# Revit family: DA330, DA420
name_source: partatom
category: Mechanical Equipment
revit_build: Autodesk Revit 2017 (Build: 20181011_1645(x64)
units: mm (PartAtom-declared; Revit-internal decimal feet)

## family parameters
Always vertical = Yes
Cut with Voids When Loaded = No
OmniClass Number = 23.40.40.11.17
OmniClass Title = Refrigerated Cases
Part Type = Normal
Room Calculation Point = No
Round Connector Dimension = Use Radius
Shared = No
Work Plane-Based = Yes

## types (1)
- D330, D420
    10" Shelf = Yes
    16" Shelf = Yes
    24" Shelf = Yes
    AIR-SWEEP FAN AMPS = 0 A
    Actual Weight = 0
    BOTTOM ELECTRICAL = Yes
    BOTTOM REFRIGERATION PIPING = Yes
    COLD WATER FILTER REQUIRED = Yes
    COLD WATER MOUNTING HEIGHT = 0"
    COLD WATER PIPE SIZE = 0"
    COLD WATER PRESSURE = 0.00 psi
    COLD WATER REGULATOR REQUIRED = Yes
    DATE = 09/03/2017
    DESIGNERS NAME = SHIDDRAMESH
    DRAIN LINE CONNECTION = SANITARY LINE CONNECTION
    DRAIN PIPING = Yes
    DUCT 1 CFM = 0 CFM
    DUCT 1 OPENING SIZE = 0"
    Default Elevation = 48"
    Defrost Num Day = 0
    Defrost Termination = -
    Defrost Type = -
    Description = SoloChill Condensing Unit
    EQUIPMENT DESCRIPTION = SoloChill Condensing Unit
    EQUIPMENT MARK = D330, D420
    Evap Temp = 0
    FAN AMPS = 1 A
    GLASS = Glass
    HOT WATER MOUNTING HEIGHT = 0"
    HOT WATER PIPE SIZE = 0"
    HOT WATER PRESSURE = 0.00 psi
    HOT WATER REGULATOR REQUIRED = Yes
    HOT WATER TEMPERATURE = 0 °F
    Height = 12 3/16"
    Item Description = SoloChill Condensing Unit
    LF STD END = Yes
    LIGHT AMPS = 0 A
    LIQUID LINE CONNECTION = LIQUID LINE CONNECTION
    LIQUID LINE RADIUS = 0"
    LOAD 1 CLASSIFICATION = Lighting
    LOAD 1 DEDICATED CIRCUIT REQUIRED = Yes
    LOAD 1 DESCRIPTION = LIGHT CONNECTION
    LOAD 1 ENERGY SETBACK REQUIRED = Yes
    LOAD 1 GROUND FAULT PROTECTION REQUIRED = Yes
    LOAD 1 ISOLATED GROUND REQUIRED = Yes
    LOAD 1 MOUNTING HEIGHT ABOVE FLOOR = 0"
    LOAD 1 NEUTRAL REQUIRED = Yes
    LOAD 1 POLES = 1
    LOAD 1 VOLTAGE = 120 V
    LOAD 1 WATTAGE = 0 W
    LOAD 2 CLASSIFICATION = Motor
    LOAD 2 DEDICATED CIRCUIT REQUIRED = Yes
    LOAD 2 DESCRIPTION = FAN CONNECTION
    LOAD 2 ENERGY SETBACK REQUIRED = Yes
    LOAD 2 GROUND FAULT PROTECTION REQUIRED = Yes
    LOAD 2 ISOLATED GROUND REQUIRED = Yes
    LOAD 2 MOUNTING HEIGHT ABOVE FLOOR = 0"
    LOAD 2 NEUTRAL REQUIRED = Yes
    LOAD 2 PLUG TYPE = HARDWIRED
    LOAD 2 POLES = 1
    LOAD 2 VOLTAGE = 120 V
    LOAD 2 WATTAGE = 0 W
    LOAD 3 CLASSIFICATION = Power
    LOAD 3 DEDICATED CIRCUIT REQUIRED = Yes
    LOAD 3 DESCRIPTION = ANTI-SWEAT CONNECTION
    LOAD 3 ENERGY SETBACK REQUIRED = Yes
    LOAD 3 GROUND FAULT PROTECTION REQUIRED = Yes
    LOAD 3 ISOLATED GROUND REQUIRED = Yes
    LOAD 3 MOUNTING HEIGHT ABOVE FLOOR = 0"
    LOAD 3 NEUTRAL REQUIRED = Yes
    LOAD 3 PLUG TYPE = HARDWIRED
    LOAD 3 POLES = 1
    LOAD 3 VOLTAGE = 120 V
    LOAD 3 WATTAGE = 0 W
    LOAD 4 CLASSIFICATION = Power
    LOAD 4 DEDICATED CIRCUIT REQUIRED = Yes
    LOAD 4 DESCRIPTION = DEFROST CONNECTION
    LOAD 4 ENERGY SETBACK REQUIRED = Yes
    LOAD 4 GROUND FAULT PROTECTION REQUIRED = Yes
    LOAD 4 ISOLATED GROUND REQUIRED = Yes
    LOAD 4 MOUNTING HEIGHT ABOVE FLOOR = 0"
    LOAD 4 NEUTRAL REQUIRED = Yes
    LOAD 4 PLUG TYPE = HARDWIRED
    LOAD 4 POLES = 1
    LOAD 4 VOLTAGE = 208 V
    LOAD 4 WATTAGE = 0 W
    LOAD 5 CLASSIFICATION = Power
    LOAD 5 DEDICATED CIRCUIT REQUIRED = Yes
    LOAD 5 DESCRIPTION = DRAIN HEATER CONNECTION
    LOAD 5 ENERGY SETBACK REQUIRED = Yes
    LOAD 5 GROUND FAULT PROTECTION REQUIRED = Yes
    LOAD 5 ISOLATED GROUND REQUIRED = Yes
    LOAD 5 MOUNTING HEIGHT ABOVE FLOOR = 0"
    LOAD 5 NEUTRAL REQUIRED = Yes
    LOAD 5 PLUG TYPE = HARDWIRED
    LOAD 5 POLES = 1
    LOAD 5 VOLTAGE = 120 V
    LOAD 5 WATTAGE = 0 W
    Legend Number = D330, D420
    Length = 43"
    Load Mbh = 0
    Manufacturer = HILL PHOENIX
    Manufacturer Model = D330, D420
    Model = D330, D420
    REAR PIPE BOX = Yes
    REAR REFRIGERATION PIPING = Yes
    RT STD END = Yes
    RUBBER BUMPER = Barker - Cart Bumper - Black Rubber
    Refrig Charge Lbs = "-"
    SANITARY MOUNTING HEIGHT = 0"
    SANITARY PIPE SIZE = 1"
    SCALE STAND OUTLET AMPS = 0 A
    SIZE OF HOT WATER HOOK-UP = 0"
    STAINLESS = GALVANIZED STEEL
    SUCTION LINE CONNECTION = SUCTION LINE CONNECTION
    SUCTION LINE RADIUS = 0"
    Supplier = Hillphoenix
    TOP ELECTRICAL = Yes
    TOP REFRIGERATION PIPING = Yes
    TOTAL AMPS = 0 A
    URL = http://www.hillphoenix.com
    VOLTS = 0 V
    Width = 20 7/16"

## geometry (parser evidence)
native form markers: Blend x10, Sweep x2
no freeform markers — native parametric forms only
